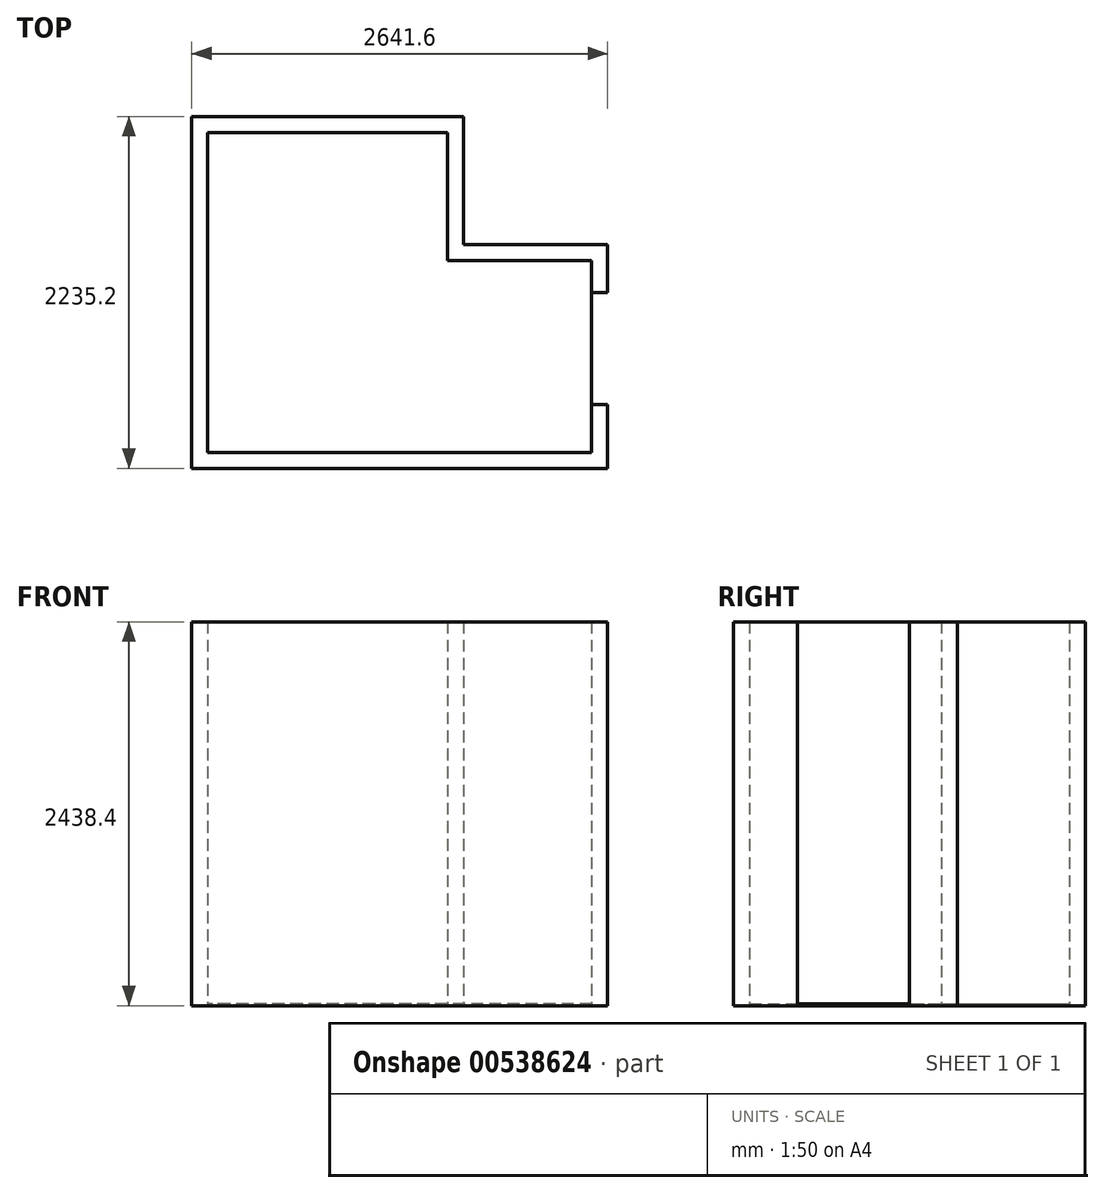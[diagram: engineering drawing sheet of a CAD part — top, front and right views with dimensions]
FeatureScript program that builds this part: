
annotation { "Feature Type Name" : "Feature", "Feature Type Description" : "" }
export const myFeature = defineFeature(function(context is Context, id is Id, definition is map)
    precondition{}
    {
        {
            var Q0;
            Q0=qCreatedBy(makeId("Top.planeOp"),FACE);
            var sketch = newSketch(context, id + "F0", { "sketchPlane" : qUnion([Q0])});
            skLineSegment(sketch, "E0.bottom", {"start": v(1219.2, -1016) * mm, "end": v(-1219.2, -1016) * mm});
            skLineSegment(sketch, "E0.top", {"start": v(304.8, 1016) * mm, "end": v(-1219.2, 1016) * mm});
            skLineSegment(sketch, "E0.left", {"start": v(1219.2, -1016) * mm, "end": v(1219.2, -711.2) * mm});
            skLineSegment(sketch, "E0.right", {"start": v(-1219.2, -1016) * mm, "end": v(-1219.2, 1016) * mm});
            skPoint(sketch, "E0.middle", {"position": v(0, 0) * mm});
            skLineSegment(sketch, "E1", {"start": v(1219.2, 203.2) * mm, "end": v(304.8, 203.2) * mm});
            skLineSegment(sketch, "E2", {"start": v(304.8, 203.2) * mm, "end": v(304.8, 1016) * mm});
            skLineSegment(sketch, "E3", {"start": v(304.8, 1016) * mm, "end": v(283.45, 1013) * mm});
            skPoint(sketch, "E4.orphan", {"position": v(1219.2, 1016) * mm});
            skLineSegment(sketch, "E5.0", {"start": v(1320.8, -1117.6) * mm, "end": v(1320.8, -711.2) * mm});
            skLineSegment(sketch, "E5.1", {"start": v(406.4, 304.8) * mm, "end": v(406.4, 1117.6) * mm});
            skLineSegment(sketch, "E5.2", {"start": v(406.4, 1117.6) * mm, "end": v(-1320.8, 1117.6) * mm});
            skLineSegment(sketch, "E5.3", {"start": v(1320.8, 304.8) * mm, "end": v(406.4, 304.8) * mm});
            skLineSegment(sketch, "E5.4", {"start": v(-1320.8, -1117.6) * mm, "end": v(-1320.8, 1117.6) * mm});
            skLineSegment(sketch, "E5.5", {"start": v(1320.8, -1117.6) * mm, "end": v(-1320.8, -1117.6) * mm});
            skLineSegment(sketch, "E6", {"start": v(1219.2, -711.2) * mm, "end": v(1320.8, -711.2) * mm});
            skLineSegment(sketch, "E7", {"start": v(1219.2, 0) * mm, "end": v(1320.8, 0) * mm});
            skLineSegment(sketch, "E8.trimOffspring", {"start": v(1320.8, 0) * mm, "end": v(1320.8, 304.8) * mm});
            skLineSegment(sketch, "E9.trimOffspring", {"start": v(1219.2, 0) * mm, "end": v(1219.2, 203.2) * mm});
            skSolve(sketch);
        }
        {
            var Q0;
            Q0=makeQuery(id+"F0.imprint","IMPRINT",FACE,{"disambiguationData":[TD([[makeQuery(id+"F0.imprint","IMPRINT",EDGE,{"derivedFrom":sQuery(id+"F0.wireOp",EDGE,"E0.bottom")}),1.0]])]});
            extrude(context, id + "F1", {"entities" : qUnion([Q0]), "depth" : 2438.4 * mm, "offsetDistance" : 30.48 * mm});
        }
        {
            var Q0;
            Q0=makeQuery(id+"F1.opExtrude","CAP_FACE",FACE,{"disambiguationData":[OSD([sQuery(id+"F0.wireOp",EDGE,"E0.bottom"),sQuery(id+"F0.wireOp",EDGE,"E0.top"),sQuery(id+"F0.wireOp",EDGE,"E0.left"),sQuery(id+"F0.wireOp",EDGE,"E0.right"),sQuery(id+"F0.wireOp",EDGE,"E1"),sQuery(id+"F0.wireOp",EDGE,"E2"),sQuery(id+"F0.wireOp",EDGE,"E5.0"),sQuery(id+"F0.wireOp",EDGE,"E5.1"),sQuery(id+"F0.wireOp",EDGE,"E5.2"),sQuery(id+"F0.wireOp",EDGE,"E5.3"),sQuery(id+"F0.wireOp",EDGE,"E5.4"),sQuery(id+"F0.wireOp",EDGE,"E5.5"),sQuery(id+"F0.wireOp",EDGE,"E6"),sQuery(id+"F0.wireOp",EDGE,"E7"),sQuery(id+"F0.wireOp",EDGE,"E8.trimOffspring"),sQuery(id+"F0.wireOp",EDGE,"E9.trimOffspring")])],"isStart":true});
            var sketch = newSketch(context, id + "F2", { "sketchPlane" : qUnion([Q0])});
            skLineSegment(sketch, "E10", {"start": v(1219.2, 1016) * mm, "end": v(1219.2, -203.2) * mm});
            skLineSegment(sketch, "E11", {"start": v(1219.2, -203.2) * mm, "end": v(304.8, -203.2) * mm});
            skLineSegment(sketch, "E12", {"start": v(304.8, -203.2) * mm, "end": v(304.8, -1016) * mm});
            skLineSegment(sketch, "E13", {"start": v(304.8, -1016) * mm, "end": v(-1219.2, -1016) * mm});
            skLineSegment(sketch, "E14", {"start": v(-1219.2, -1016) * mm, "end": v(-1219.2, 1016) * mm});
            skLineSegment(sketch, "E15", {"start": v(-1219.2, 1016) * mm, "end": v(1219.2, 1016) * mm});
            skSolve(sketch);
        }
        {
            var Q0;
            {var subQ0=sQuery(id+"F2.wireOp",EDGE,"E11");Q0=makeQuery(id+"F2.imprint","IMPRINT",FACE,{"disambiguationData":[TD([[makeQuery(id+"F2.imprint","IMPRINT",EDGE,{"derivedFrom":subQ0}),-1.0]])]});}
            extrude(context, id + "F3", {"entities" : qUnion([Q0]), "oppositeDirection" : true, "depth" : 12.7 * mm, "offsetDistance" : 30.48 * mm});
        }
    });
